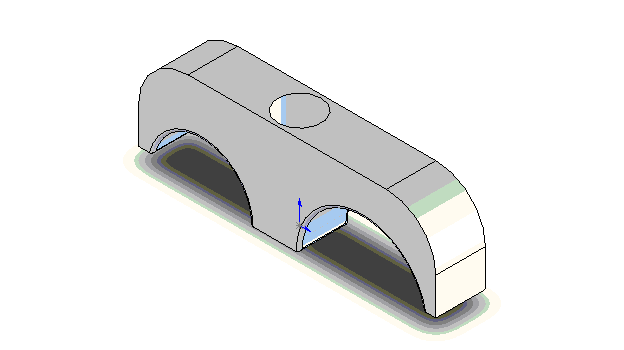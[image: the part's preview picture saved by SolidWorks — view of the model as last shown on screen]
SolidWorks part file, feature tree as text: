
SOLIDWORKS PART (.sldprt)
format: sldprt  version: not decoded by parser v0  size: 239,616 bytes
history: native  units: mm
features: sketch x3, fillet x2, extrude x1, hole x1 (+11 scaffold rows collapsed)
feature tree (18):
  scaffold x11  (default folders/planes/origin — collapsed)
  sketch  "Sketch1"  dims[c1.D1=~29.818825mm c1.D4=12.7mm c1.D5=16.002mm c2.D1=3.175mm c2.D2=3.175mm c2.D3=25.4mm c2.D6=76.2mm c2.D7=41.275mm c2.D8=~0.79375mm c2.D9=~0.79375mm c2.D10=19.05mm c3.D2=60.325mm c3.D3=25.4mm c3.D8=22.225mm c4.D3=25.4mm]
  extrude  "Extrude1"  Depth=12.7mm
  fillet  "Fillet1"  Radius=12.7mm
  fillet  "Fillet2"  Radius=0.762mm
  hole  "CBORE for 1/4 Socket Head Cap Screw1"  Diameter=6.7564mm Depth=25.4mm
  sketch  "3DSketch1"  dims[D1=41.275mm D2=6.35mm]
  sketch  "Sketch2"  dims[hole-wizard template sketch: 44 standard entries collapsed; hole parameters kept: c12.C'Bore Depth=7.9375mm]
decode coverage: 7 of 7 modeling features carry decoded parameters
note: ~ marks probable driven/reference dimensions
note: suppression state not decoded; provenance and decode notes live in map.json
